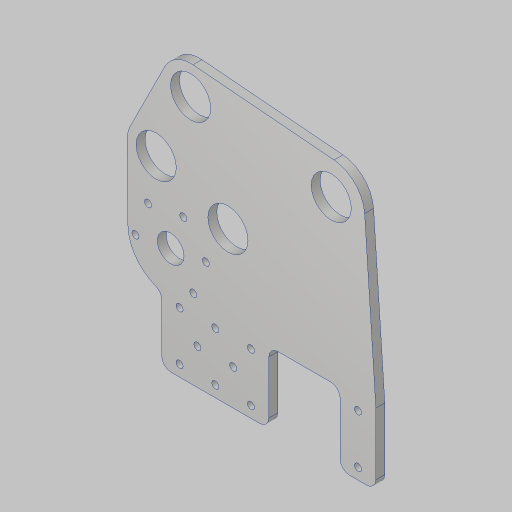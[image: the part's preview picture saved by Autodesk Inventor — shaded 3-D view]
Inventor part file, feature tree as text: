
AUTODESK INVENTOR PART (.ipt)
format: ipt  version: 2023.5 (Build 275446000, 446)  size: 272,896 bytes
history: native  units: in
note: dims shown in document units (in); Inventor stores cm internally (conversion verified against a paired STEP export)
features: sketch x3, extrude x3, hole x2, fillet x2, projected_geometry x1
ambient origin geometry x8: Origin, YZ Plane, XZ Plane, XY Plane, X Axis, Y Axis, Z Axis, Center Point
bodies: Solid1 (feature_tree)
feature tree (11):
  sketch  "Sketch1"  dims[d0=6.0in d1=2.0in]
  sketch  "Sketch2"  dims[d2=1.375in d3=0.5in d4=1.25in]
  extrude  "Extrusion1"  Depth=2.0in
  hole  "Hole1"  [1 undecoded]
  fillet  "Fillet1"  Radius=1.25in
  sketch  "Sketch4"  dims[d5=1.25in d6=1.375in d7=1.0in d8=0.375in d9=0.5in d10=0.5in d11=0.5in d12=0.5in d13=0.5in d14=4.38in d15=5.0in d16=3.0in d17=1.125in d18=0.375in d20=0.375in d21=0.375in d22=0.25in d23=0.0in d24=0.201in d25=0.75in d26=0.375in d27=0.25in d28=0.5635in d29=1.0in d30=0.8108in d31=6.5in d32=0.75in d33=0.26in d45=2.0in d46=2.4in d47=0.75in d48=0.5in d49=3.6in d50=0.25in d52=8.0in d53=2.0in d54=3.0in d55=1.125in d56=0.25in d57=1.0in d58=3.3in d59=2.275in d60=1.0in d61=3.3in d64=0.25in d65=0.25in d66=1.0in d67=0.0in d68=2.3622in d70=360.0deg d72=0.0in d73=0.0in d74=0.201in d75=0.75in d76=0.385in d77=0.25in d78=0.5635in d79=1.0in d80=0.8108in d82=3.342in d83=0.58in d85=0.26in d86=1.114in d92=3.8082in d93=6.2007in d94=1.4328in d95=5.0373in]
  extrude  "Extrusion3"  Depth=0.26in
  extrude  "Extrusion4"  Depth=1.0in
  hole  "Hole2"  [1 undecoded]
  fillet  "Fillet4"  Radius=0.5in
  projected_geometry  "Project Cut Edges2"
note: 2 required parameter values undecoded (feature->parameter linkage not recoverable at this tier; creation-order binding heuristic only, values carry confidence <= 0.55)
